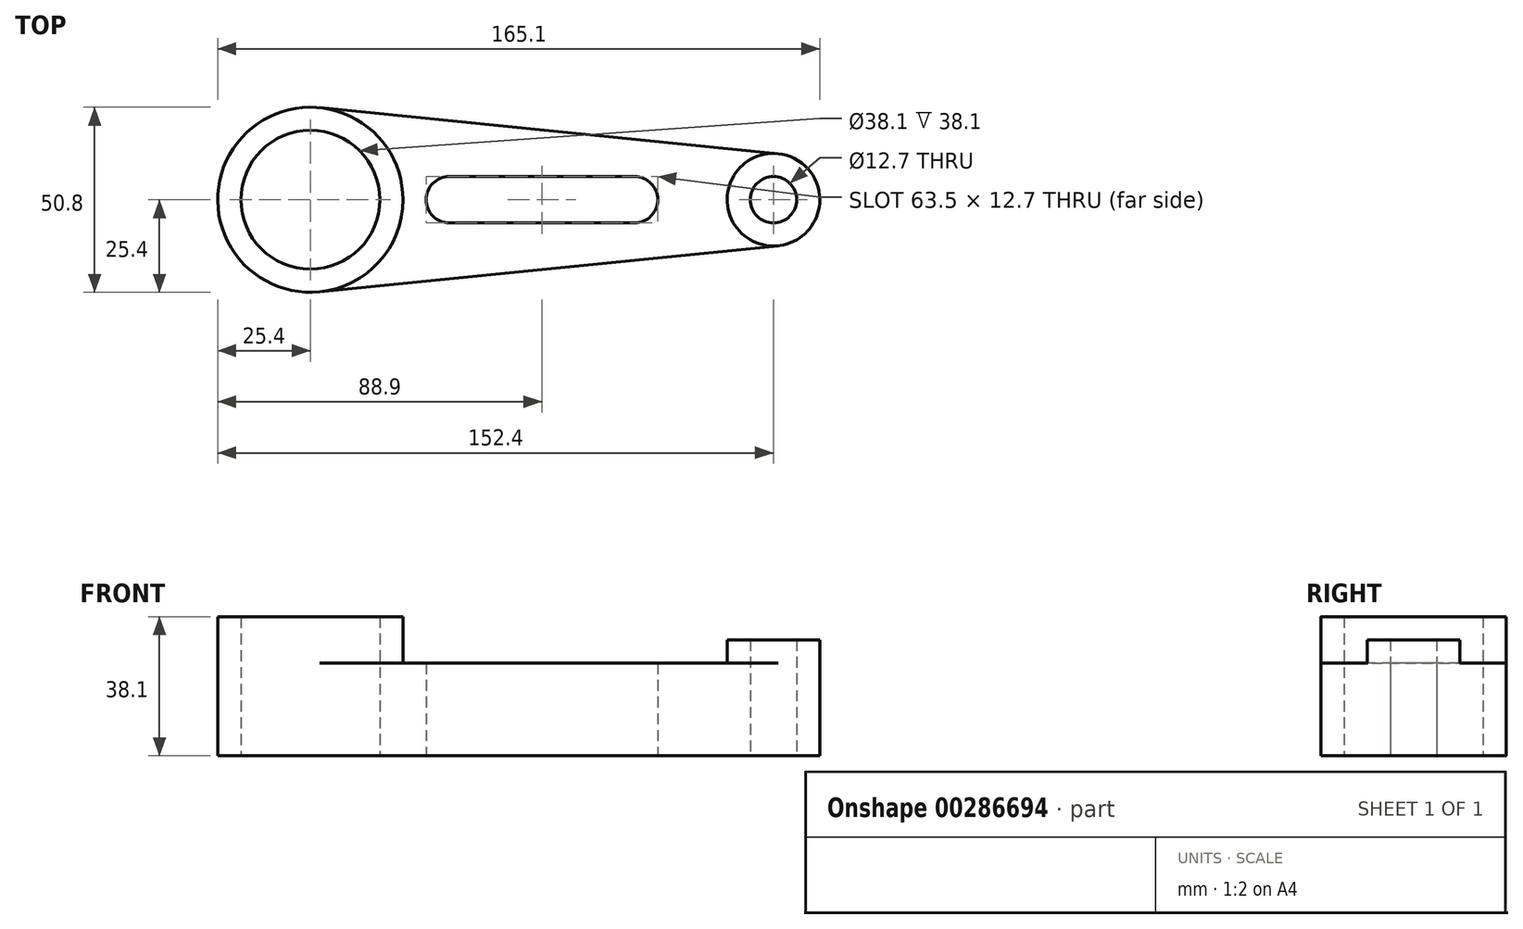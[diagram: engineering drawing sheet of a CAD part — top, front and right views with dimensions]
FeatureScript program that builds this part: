
annotation { "Feature Type Name" : "Feature", "Feature Type Description" : "" }
export const myFeature = defineFeature(function(context is Context, id is Id, definition is map)
    precondition{}
    {
        {
            var Q0;
            Q0=qCreatedBy(makeId("Top.planeOp"),FACE);
            var sketch = newSketch(context, id + "F0", { "sketchPlane" : qUnion([Q0])});
            skArc(sketch, "E0", {"start": v(0, 6.35) * mm, "mid": v(-6.35, 0) * mm, "end": v(0, -6.35) * mm});
            skArc(sketch, "E1", {"start": v(50.8, -6.35) * mm, "mid": v(57.15, 0) * mm, "end": v(50.8, 6.35) * mm});
            skCircle(sketch, "E2", {"center": v(-38.1, 0) * mm, "radius": 19.05 * mm});
            skCircle(sketch, "E3", {"center": v(-38.1, 0) * mm, "radius": 25.4 * mm});
            skCircle(sketch, "E4", {"center": v(88.9, 0) * mm, "radius": 6.35 * mm});
            skCircle(sketch, "E5", {"center": v(88.9, 0) * mm, "radius": 12.7 * mm});
            skLineSegment(sketch, "E6", {"start": v(0, 6.35) * mm, "end": v(50.8, 6.35) * mm});
            skLineSegment(sketch, "E7", {"start": v(0, -6.35) * mm, "end": v(50.8, -6.35) * mm});
            skLineSegment(sketch, "E8", {"start": v(-38.1, 0) * mm, "end": v(88.9, 0) * mm, "construction": true});
            skLineSegment(sketch, "E9", {"start": v(-35.56, 25.27) * mm, "end": v(90.17, 12.64) * mm});
            skLineSegment(sketch, "E10", {"start": v(-35.56, -25.27) * mm, "end": v(90.17, -12.64) * mm});
            skSolve(sketch);
        }
        {
            var Q0;
            Q0=makeQuery(id+"F0.imprint","IMPRINT",FACE,{"disambiguationData":[TD([[makeQuery(id+"F0.imprint","IMPRINT",EDGE,{"derivedFrom":sQuery(id+"F0.wireOp",EDGE,"E0")}),-1.0]])]});
            extrude(context, id + "F1", {"entities" : qUnion([Q0]), "depth" : 25.4 * mm});
        }
        {
            var Q0;
            Q0=makeQuery(id+"F0.imprint","IMPRINT",FACE,{"disambiguationData":[TD([[makeQuery(id+"F0.imprint","IMPRINT",EDGE,{"derivedFrom":sQuery(id+"F0.wireOp",EDGE,"E2")}),-1.0]])]});
            extrude(context, id + "F2", {"entities" : qUnion([Q0]), "operationType" : NewBodyOperationType.ADD, "depth" : 38.1 * mm});
        }
        {
            var Q0;
            Q0=makeQuery(id+"F0.imprint","IMPRINT",FACE,{"disambiguationData":[TD([[makeQuery(id+"F0.imprint","IMPRINT",EDGE,{"derivedFrom":sQuery(id+"F0.wireOp",EDGE,"E4")}),-1.0]])]});
            extrude(context, id + "F3", {"entities" : qUnion([Q0]), "operationType" : NewBodyOperationType.ADD, "depth" : 31.75 * mm});
        }
    });
